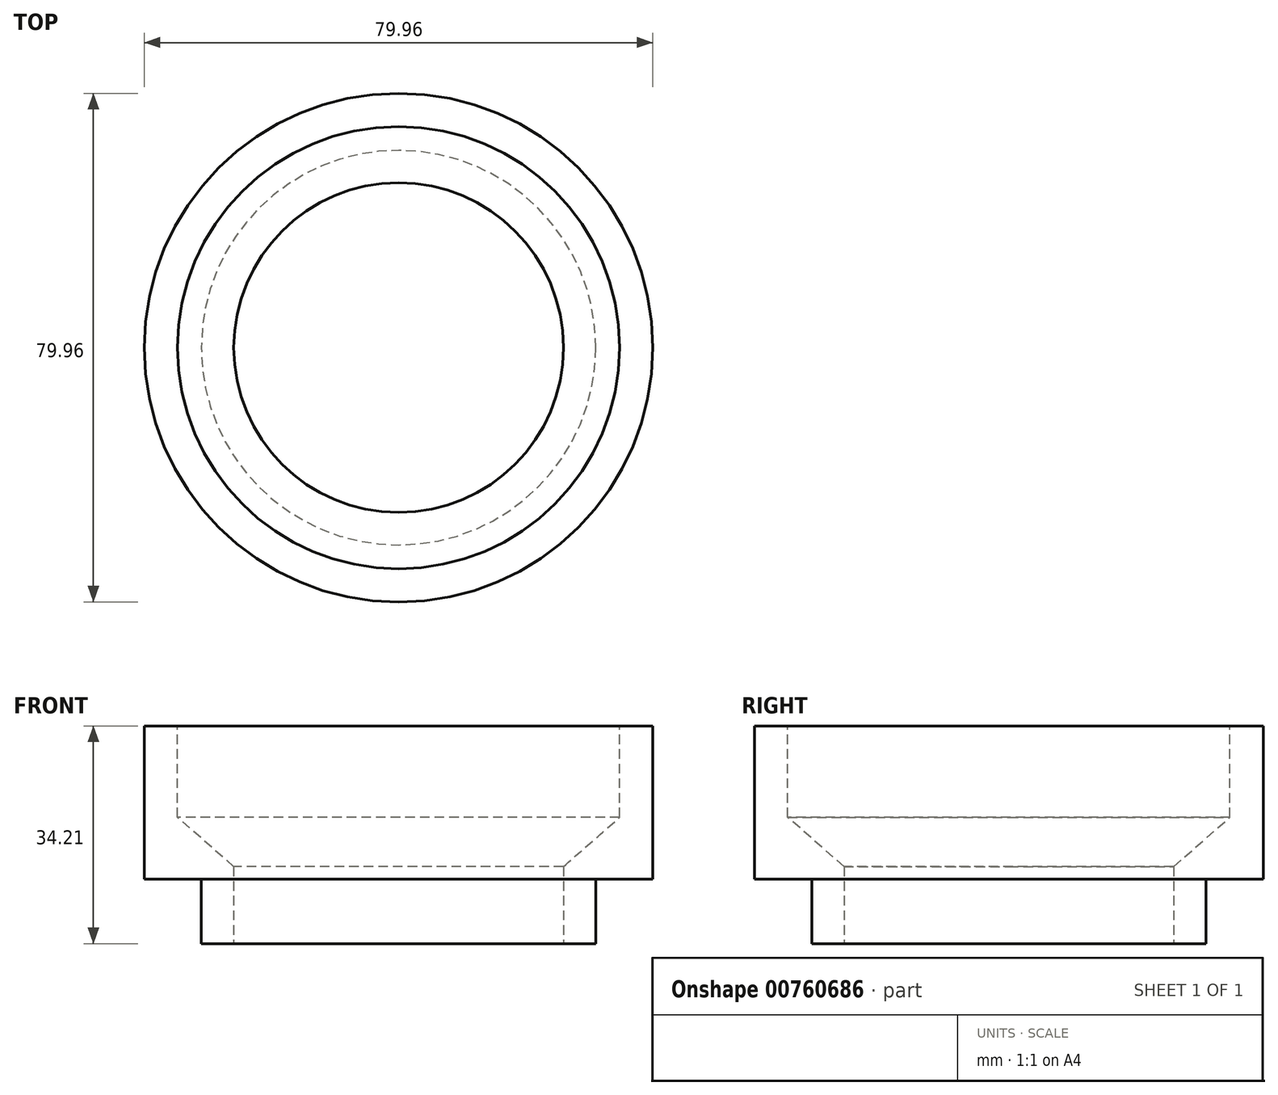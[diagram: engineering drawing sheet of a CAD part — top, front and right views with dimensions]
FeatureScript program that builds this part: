
annotation { "Feature Type Name" : "Feature", "Feature Type Description" : "" }
export const myFeature = defineFeature(function(context is Context, id is Id, definition is map)
    precondition{}
    {
        {
            var Q0;
            Q0=qCreatedBy(makeId("Front.planeOp"),FACE);
            var sketch = newSketch(context, id + "F0", { "sketchPlane" : qUnion([Q0])});
            skLineSegment(sketch, "E0", {"start": v(0, 0) * mm, "end": v(31, 0) * mm});
            skLineSegment(sketch, "E1", {"start": v(31, 0) * mm, "end": v(31, 10.13) * mm});
            skLineSegment(sketch, "E2", {"start": v(31, 10.13) * mm, "end": v(39.98, 10.13) * mm});
            skLineSegment(sketch, "E3", {"start": v(39.98, 10.13) * mm, "end": v(39.98, 34.21) * mm});
            skLineSegment(sketch, "E4", {"start": v(39.98, 34.21) * mm, "end": v(34.76, 34.21) * mm});
            skLineSegment(sketch, "E5", {"start": v(34.76, 34.21) * mm, "end": v(34.76, 19.86) * mm});
            skLineSegment(sketch, "E6", {"start": v(34.76, 19.86) * mm, "end": v(23.67, 10.13) * mm});
            skLineSegment(sketch, "E7", {"start": v(0, 10.13) * mm, "end": v(0, 0) * mm});
            skLineSegment(sketch, "E8", {"start": v(0, 10.13) * mm, "end": v(23.67, 10.13) * mm});
            skSolve(sketch);
        }
        {
            var Q0;
            Q0 = qSketchRegion(id + "F0", true);
            var Q1;
            Q1=sQuery(id+"F0.wireOp",EDGE,"E7");
            revolve(context, id + "F1", {"surfaceOperationType" : NewSurfaceOperationType.NEW, "entities" : qUnion([Q0]), "axis" : qUnion([Q1]), "revolveType" : RevolveType.FULL});
        }
        {
            var Q0;
            Q0=qCreatedBy(makeId("Top.planeOp"),FACE);
            var sketch = newSketch(context, id + "F2", { "sketchPlane" : qUnion([Q0])});
            skCircle(sketch, "E9", {"center": v(0, 0) * mm, "radius": 25.92 * mm});
            skSolve(sketch);
        }
        {
            var Q0;
            Q0 = qSketchRegion(id + "F2", true);
            extrude(context, id + "F3", {"entities" : qUnion([Q0]), "operationType" : NewBodyOperationType.REMOVE, "depth" : 25 * mm, "offsetDistance" : 25 * mm});
        }
    });
